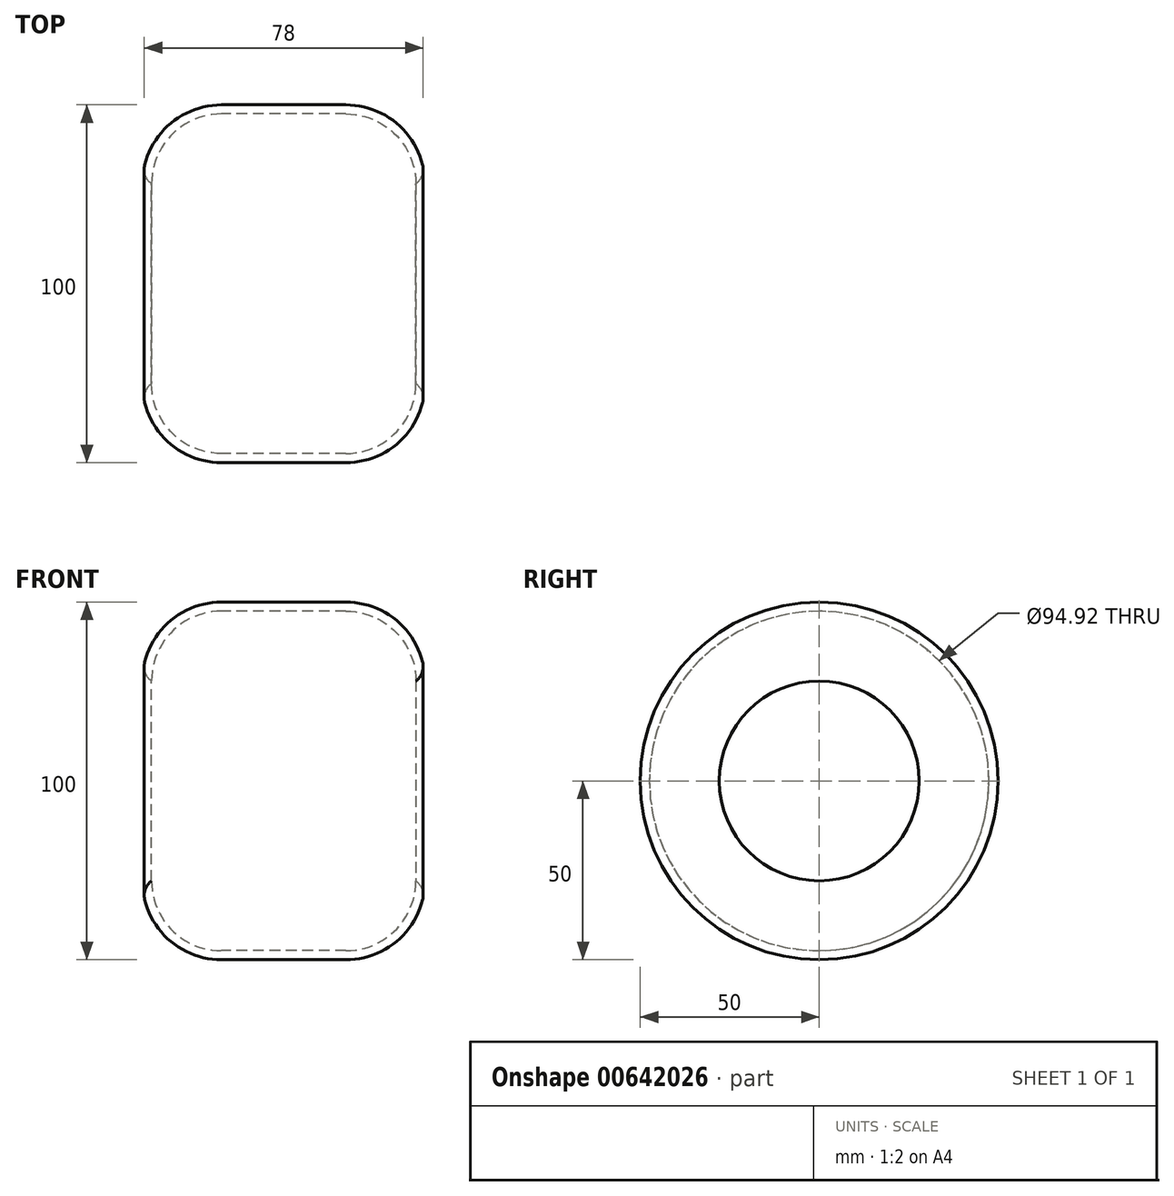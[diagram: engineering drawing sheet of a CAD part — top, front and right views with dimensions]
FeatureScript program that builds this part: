
annotation { "Feature Type Name" : "Feature", "Feature Type Description" : "" }
export const myFeature = defineFeature(function(context is Context, id is Id, definition is map)
    precondition{}
    {
        {
            var Q0;
            Q0=qCreatedBy(makeId("Right.planeOp"),FACE);
            var sketch = newSketch(context, id + "F0", { "sketchPlane" : qUnion([Q0])});
            skCircle(sketch, "E0", {"center": v(0, 0) * mm, "radius": 50 * mm});
            skSolve(sketch);
        }
        {
            var Q0;
            Q0=makeQuery(id+"F0.imprint","IMPRINT",FACE,{"disambiguationData":[TD([[makeQuery(id+"F0.imprint","IMPRINT",EDGE,{"derivedFrom":sQuery(id+"F0.wireOp",EDGE,"E0")}),1.0]])]});
            extrude(context, id + "F1", {"entities" : qUnion([Q0]), "depth" : 79 * mm, "offsetDistance" : 25.4 * mm});
        }
        {
            var Q0;
            Q0=makeQuery(id+"F1.opExtrude","CAP_FACE",FACE,{"disambiguationData":[OSD([sQuery(id+"F0.wireOp",EDGE,"E0")])],"isStart":false});
            var Q1;
            Q1=makeQuery(id+"F1.opExtrude","CAP_FACE",FACE,{"disambiguationData":[OSD([sQuery(id+"F0.wireOp",EDGE,"E0")])],"isStart":true});
            var Q2;
            Q2=makeQuery(id+"F1.opExtrude","SWEPT_FACE",FACE,{"disambiguationData":[OSD([sQuery(id+"F0.wireOp",EDGE,"E0")])]});
            fillet(context, id + "F2", {"entities" : qUnion([Q0, Q1, Q2]), "radius" : 22.08 * mm, "tangentPropagation" : true, "allowEdgeOverflow" : false});
        }
        {
            var Q0;
            Q0=makeQuery(id+"F1.opExtrude","CAP_FACE",FACE,{"disambiguationData":[OSD([sQuery(id+"F0.wireOp",EDGE,"E0")])],"isStart":false});
            var Q1;
            Q1=makeQuery(id+"F1.opExtrude","CAP_FACE",FACE,{"disambiguationData":[OSD([sQuery(id+"F0.wireOp",EDGE,"E0")])],"isStart":true});
            shell(context, id + "F3", {"entities" : qUnion([Q0, Q1]), "thickness" : 2.54 * mm});
        }
        {
            var Q0;
            {var subQ0=sQuery(id+"F0.wireOp",EDGE,"E0");Q0=makeQuery(id+"F2.opFillet","BLEND_FACE",FACE,{"disambiguationData":[OSD([subQ0]),TDD([makeQuery(id+"F1.opExtrude","CAP_EDGE",EDGE,{"disambiguationData":[OSD([subQ0])],"isStart":true})])]});}
            var Q1;
            {var subQ0=sQuery(id+"F0.wireOp",EDGE,"E0");Q1=makeQuery(id+"F2.opFillet","BLEND_FACE",FACE,{"disambiguationData":[OSD([subQ0]),TDD([makeQuery(id+"F1.opExtrude","CAP_EDGE",EDGE,{"disambiguationData":[OSD([subQ0])],"isStart":false})])]});}
            fillet(context, id + "F4", {"entities" : qUnion([Q0, Q1]), "radius" : 5.08 * mm, "tangentPropagation" : true, "allowEdgeOverflow" : false});
        }
    });
